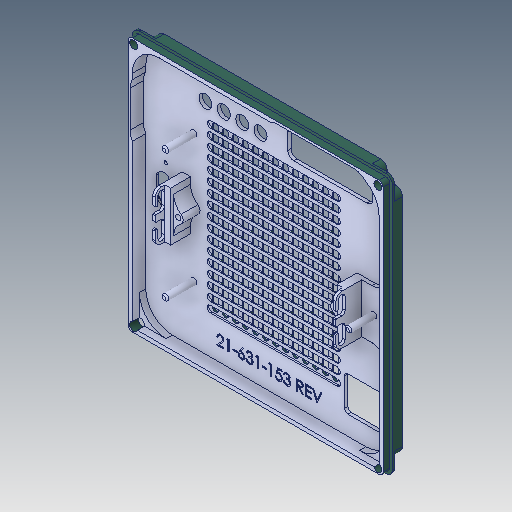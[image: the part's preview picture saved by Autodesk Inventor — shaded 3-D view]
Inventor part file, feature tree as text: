
AUTODESK INVENTOR PART (.ipt)
format: ipt  version: 2019 (Build 230136000, 136)  size: 1,181,184 bytes
history: native  units: in
note: dims shown in document units (in); Inventor stores cm internally (conversion verified against a paired STEP export)
features: chamfer x1
ambient origin geometry x8: Origin, YZ Plane, XZ Plane, XY Plane, X Axis, Y Axis, Z Axis, Center Point
bodies: Solid1 (feature_tree)
feature tree (1):
  chamfer  "Chamfer4"  [1 undecoded]
note: 1 required parameter value undecoded (feature->parameter linkage not recoverable at this tier; creation-order binding heuristic only, values carry confidence <= 0.55)
